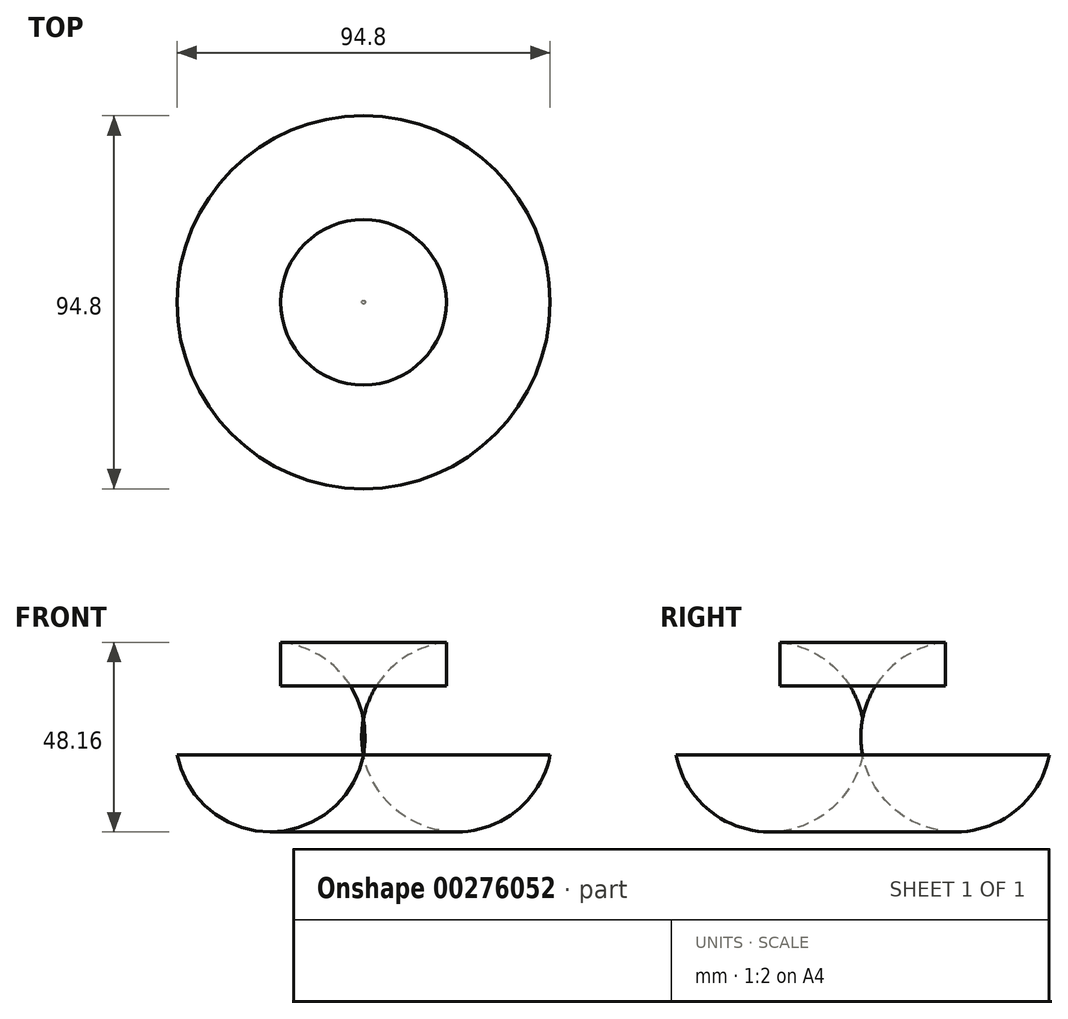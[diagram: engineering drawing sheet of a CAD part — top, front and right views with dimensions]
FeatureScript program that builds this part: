
annotation { "Feature Type Name" : "Feature", "Feature Type Description" : "" }
export const myFeature = defineFeature(function(context is Context, id is Id, definition is map)
    precondition{}
    {
        {
            var Q0;
            Q0=qCreatedBy(makeId("Front.planeOp"),FACE);
            var sketch = newSketch(context, id + "F1", { "sketchPlane" : qUnion([Q0])});
            skLineSegment(sketch, "E0", {"start": v(0, 0) * mm, "end": v(21.03, 0) * mm});
            skLineSegment(sketch, "E1", {"start": v(21.03, 0) * mm, "end": v(21.03, 11.03) * mm});
            skLineSegment(sketch, "E2", {"start": v(41.37, 11.18) * mm, "end": v(41.37, 11.18) * mm});
            skLineSegment(sketch, "E3", {"start": v(47.4, -17.64) * mm, "end": v(47.4, -17.64) * mm});
            skLineSegment(sketch, "E4", {"start": v(47.4, -17.64) * mm, "end": v(0, -17.64) * mm});
            skLineSegment(sketch, "E5", {"start": v(0, -17.64) * mm, "end": v(0, -17.64) * mm});
            skLineSegment(sketch, "E6", {"start": v(0, -17.64) * mm, "end": v(0, 0) * mm});
            skArc(sketch, "E7", {"start": v(47.4, -17.64) * mm, "mid": v(41.48, 3.37) * mm, "end": v(21.03, 11.03) * mm});
            skPoint(sketch, "E8", {"position": v(23.7, -17.64) * mm});
            skLineSegment(sketch, "E9", {"start": v(-1.83, 0) * mm, "end": v(-1.83, -17.7) * mm});
            skSolve(sketch);
        }
        {
            var Q0;
            Q0=makeQuery(id+"F1.imprint","IMPRINT",FACE,{"disambiguationData":[TD([[makeQuery(id+"F1.imprint","IMPRINT",EDGE,{"derivedFrom":sQuery(id+"F1.wireOp",EDGE,"E0")}),-1.0]])]});
            var Q1;
            Q1=sQuery(id+"F1.wireOp",EDGE,"E0");
            var Q2;
            Q2=sQuery(id+"F1.wireOp",EDGE,"E4");
            var Q3;
            Q3=sQuery(id+"F1.wireOp",EDGE,"E7");
            var Q4;
            Q4=sQuery(id+"F1.wireOp",EDGE,"E1");
            var Q5;
            Q5=sQuery(id+"F1.wireOp",EDGE,"E6");
            var Q6;
            Q6=sQuery(id+"F1.wireOp",EDGE,"E6");
            revolve(context, id + "F2", {"entities" : qUnion([Q0]), "surfaceEntities" : qUnion([Q1, Q2, Q3, Q4, Q5]), "axis" : qUnion([Q6]), "revolveType" : RevolveType.FULL});
        }
    });
